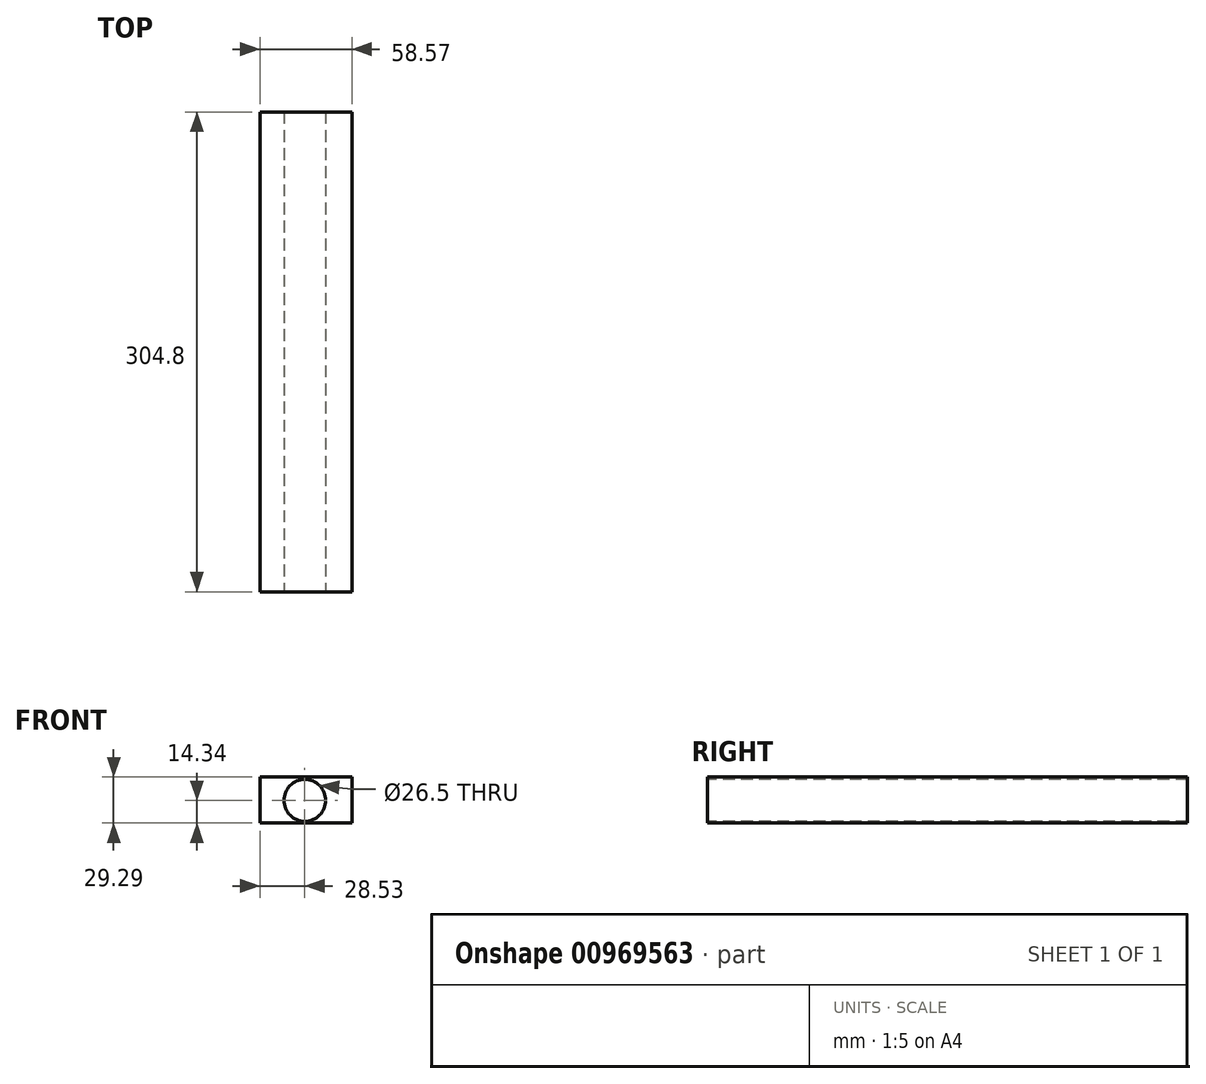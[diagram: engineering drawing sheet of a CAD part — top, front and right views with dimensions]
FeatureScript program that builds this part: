
annotation { "Feature Type Name" : "Feature", "Feature Type Description" : "" }
export const myFeature = defineFeature(function(context is Context, id is Id, definition is map)
    precondition{}
    {
        {
            var Q0;
            Q0=qCreatedBy(makeId("Front.planeOp"),FACE);
            var sketch = newSketch(context, id + "F0", { "sketchPlane" : qUnion([Q0])});
            skLineSegment(sketch, "E0.bottom", {"start": v(30.04, -14.34) * mm, "end": v(-28.53, -14.34) * mm});
            skLineSegment(sketch, "E0.top", {"start": v(30.04, 14.95) * mm, "end": v(-28.53, 14.95) * mm});
            skLineSegment(sketch, "E0.left", {"start": v(30.04, -14.34) * mm, "end": v(30.04, 14.95) * mm});
            skLineSegment(sketch, "E0.right", {"start": v(-28.53, -14.34) * mm, "end": v(-28.53, 14.95) * mm});
            skPoint(sketch, "E0.middle", {"position": v(0.75, 0.3) * mm});
            skSolve(sketch);
        }
        {
            var Q0;
            Q0=qCreatedBy(makeId("Front.planeOp"),FACE);
            var sketch = newSketch(context, id + "F1", { "sketchPlane" : qUnion([Q0])});
            skSolve(sketch);
        }
        {
            var Q0;
            Q0 = qSketchRegion(id + "F1", true);
            var Q1;
            Q1=makeQuery(id+"F0.imprint","IMPRINT",FACE,{"disambiguationData":[TD([[makeQuery(id+"F0.imprint","IMPRINT",EDGE,{"derivedFrom":sQuery(id+"F0.wireOp",EDGE,"E0.bottom")}),-1.0]])]});
            extrude(context, id + "F2", {"entities" : qUnion([Q0, Q1]), "depth" : 304.8 * mm, "offsetDistance" : 25.4 * mm});
        }
        {
            var Q0;
            Q0=makeQuery(id+"F2.opExtrude","CAP_FACE",FACE,{"disambiguationData":[OSD([sQuery(id+"F0.wireOp",EDGE,"E0.bottom"),sQuery(id+"F0.wireOp",EDGE,"E0.top"),sQuery(id+"F0.wireOp",EDGE,"E0.left"),sQuery(id+"F0.wireOp",EDGE,"E0.right")])],"isStart":false});
            var sketch = newSketch(context, id + "F3", { "sketchPlane" : qUnion([Q0])});
            skCircle(sketch, "E1", {"center": v(0, 0) * mm, "radius": 13.25 * mm});
            skSolve(sketch);
        }
        {
            var Q0;
            Q0=makeQuery(id+"F3.imprint","IMPRINT",FACE,{"disambiguationData":[TD([[makeQuery(id+"F3.imprint","IMPRINT",EDGE,{"derivedFrom":sQuery(id+"F3.wireOp",EDGE,"E1")}),1.0]])]});
            var Q1;
            Q1 = qSketchRegion(id + "F3", true);
            extrude(context, id + "F4", {"entities" : qUnion([Q0, Q1]), "operationType" : NewBodyOperationType.REMOVE, "flatOperationType" : FlatOperationType.REMOVE, "oppositeDirection" : true, "depth" : 304.8 * mm, "offsetDistance" : 25.4 * mm, "domain" : OperationDomain.MODEL});
        }
    });
